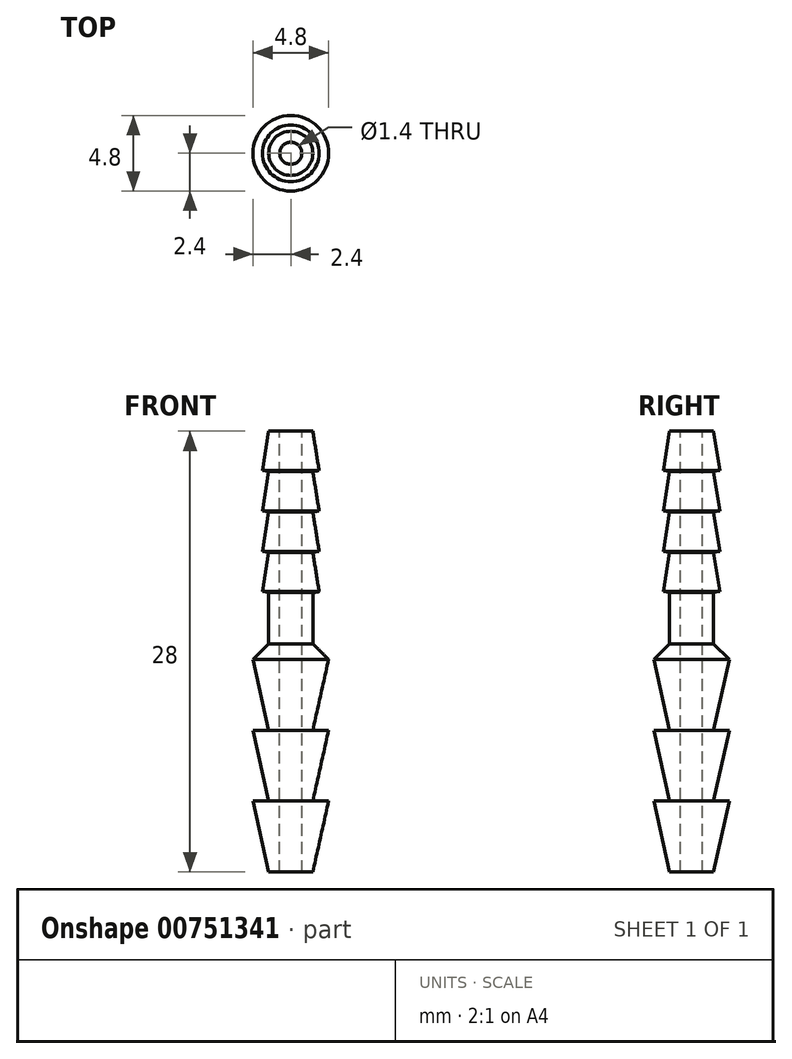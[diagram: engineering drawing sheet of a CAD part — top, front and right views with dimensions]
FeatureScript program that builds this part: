
annotation { "Feature Type Name" : "Feature", "Feature Type Description" : "" }
export const myFeature = defineFeature(function(context is Context, id is Id, definition is map)
    precondition{}
    {
        {
            var Q0;
            Q0=qCreatedBy(makeId("Front.planeOp"),FACE);
            var sketch = newSketch(context, id + "F0", { "sketchPlane" : qUnion([Q0])});
            skLineSegment(sketch, "E0.bottom", {"start": v(0.7, 14) * mm, "end": v(1.4, 14) * mm});
            skLineSegment(sketch, "E0.top", {"start": v(0.7, -14) * mm, "end": v(1.4, -14) * mm});
            skLineSegment(sketch, "E0.left", {"start": v(0.7, 14) * mm, "end": v(0.7, -14) * mm});
            skLineSegment(sketch, "E0.right", {"start": v(1.4, 14) * mm, "end": v(1.4, -14) * mm});
            skLineSegment(sketch, "E1", {"start": v(1.4, -14) * mm, "end": v(2.4, -9.5) * mm});
            skLineSegment(sketch, "E2", {"start": v(2.4, -9.5) * mm, "end": v(1.4, -9.5) * mm});
            skLineSegment(sketch, "E3", {"start": v(1.4, -9.5) * mm, "end": v(2.4, -5) * mm});
            skLineSegment(sketch, "E4", {"start": v(2.4, -5) * mm, "end": v(1.4, -5) * mm});
            skLineSegment(sketch, "E5", {"start": v(1.4, -5) * mm, "end": v(2.4, -0.5) * mm});
            skLineSegment(sketch, "E6", {"start": v(2.4, -0.5) * mm, "end": v(1.4, -0.5) * mm});
            skLineSegment(sketch, "E7", {"start": v(1.4, 14) * mm, "end": v(1.8, 11.5) * mm});
            skLineSegment(sketch, "E8", {"start": v(1.8, 11.5) * mm, "end": v(1.4, 11.44) * mm});
            skLineSegment(sketch, "E9", {"start": v(1.4, 11.44) * mm, "end": v(1.8, 8.94) * mm});
            skLineSegment(sketch, "E10", {"start": v(1.8, 8.94) * mm, "end": v(1.4, 8.87) * mm});
            skLineSegment(sketch, "E11", {"start": v(1.4, 8.87) * mm, "end": v(1.8, 6.37) * mm});
            skLineSegment(sketch, "E12", {"start": v(1.8, 6.37) * mm, "end": v(1.4, 6.3) * mm});
            skLineSegment(sketch, "E13", {"start": v(1.4, 6.3) * mm, "end": v(1.8, 3.8) * mm});
            skLineSegment(sketch, "E14", {"start": v(1.8, 3.8) * mm, "end": v(1.4, 3.74) * mm});
            skLineSegment(sketch, "E15", {"start": v(2.4, -0.5) * mm, "end": v(1.4, 0.5) * mm});
            skLineSegment(sketch, "E16", {"start": v(0, 19.74) * mm, "end": v(0, -18.98) * mm});
            skSolve(sketch);
        }
        {
            var Q0;
            {var subQ8=sQuery(id+"F0.wireOp",EDGE,"E0.bottom");Q0=makeQuery(id+"F0.imprint","IMPRINT",FACE,{"disambiguationData":[TD([[makeQuery(id+"F0.imprint","IMPRINT",EDGE,{"derivedFrom":subQ8}),-1.0]])]});}
            var Q1;
            {var subQ0=sQuery(id+"F0.wireOp",EDGE,"E7");Q1=makeQuery(id+"F0.imprint","IMPRINT",FACE,{"disambiguationData":[TD([[makeQuery(id+"F0.imprint","IMPRINT",EDGE,{"derivedFrom":subQ0}),-1.0]])]});}
            var Q2;
            {var subQ0=sQuery(id+"F0.wireOp",EDGE,"E9");Q2=makeQuery(id+"F0.imprint","IMPRINT",FACE,{"disambiguationData":[TD([[makeQuery(id+"F0.imprint","IMPRINT",EDGE,{"derivedFrom":subQ0}),-1.0]])]});}
            var Q3;
            {var subQ0=sQuery(id+"F0.wireOp",EDGE,"E11");Q3=makeQuery(id+"F0.imprint","IMPRINT",FACE,{"disambiguationData":[TD([[makeQuery(id+"F0.imprint","IMPRINT",EDGE,{"derivedFrom":subQ0}),-1.0]])]});}
            var Q4;
            {var subQ0=sQuery(id+"F0.wireOp",EDGE,"E13");Q4=makeQuery(id+"F0.imprint","IMPRINT",FACE,{"disambiguationData":[TD([[makeQuery(id+"F0.imprint","IMPRINT",EDGE,{"derivedFrom":subQ0}),-1.0]])]});}
            var Q5;
            {var subQ0=sQuery(id+"F0.wireOp",EDGE,"E6");Q5=makeQuery(id+"F0.imprint","IMPRINT",FACE,{"disambiguationData":[TD([[makeQuery(id+"F0.imprint","IMPRINT",EDGE,{"derivedFrom":subQ0}),-1.0]])]});}
            var Q6;
            {var subQ0=sQuery(id+"F0.wireOp",EDGE,"E5");Q6=makeQuery(id+"F0.imprint","IMPRINT",FACE,{"disambiguationData":[TD([[makeQuery(id+"F0.imprint","IMPRINT",EDGE,{"derivedFrom":subQ0}),1.0]])]});}
            var Q7;
            {var subQ0=sQuery(id+"F0.wireOp",EDGE,"E3");Q7=makeQuery(id+"F0.imprint","IMPRINT",FACE,{"disambiguationData":[TD([[makeQuery(id+"F0.imprint","IMPRINT",EDGE,{"derivedFrom":subQ0}),1.0]])]});}
            var Q8;
            {var subQ0=sQuery(id+"F0.wireOp",EDGE,"E1");Q8=makeQuery(id+"F0.imprint","IMPRINT",FACE,{"disambiguationData":[TD([[makeQuery(id+"F0.imprint","IMPRINT",EDGE,{"derivedFrom":subQ0}),1.0]])]});}
            var Q9;
            Q9=sQuery(id+"F0.wireOp",EDGE,"E16");
            revolve(context, id + "F1", {"surfaceOperationType" : NewSurfaceOperationType.NEW, "entities" : qUnion([Q0, Q1, Q2, Q3, Q4, Q5, Q6, Q7, Q8]), "axis" : qUnion([Q9]), "revolveType" : RevolveType.FULL});
        }
    });
